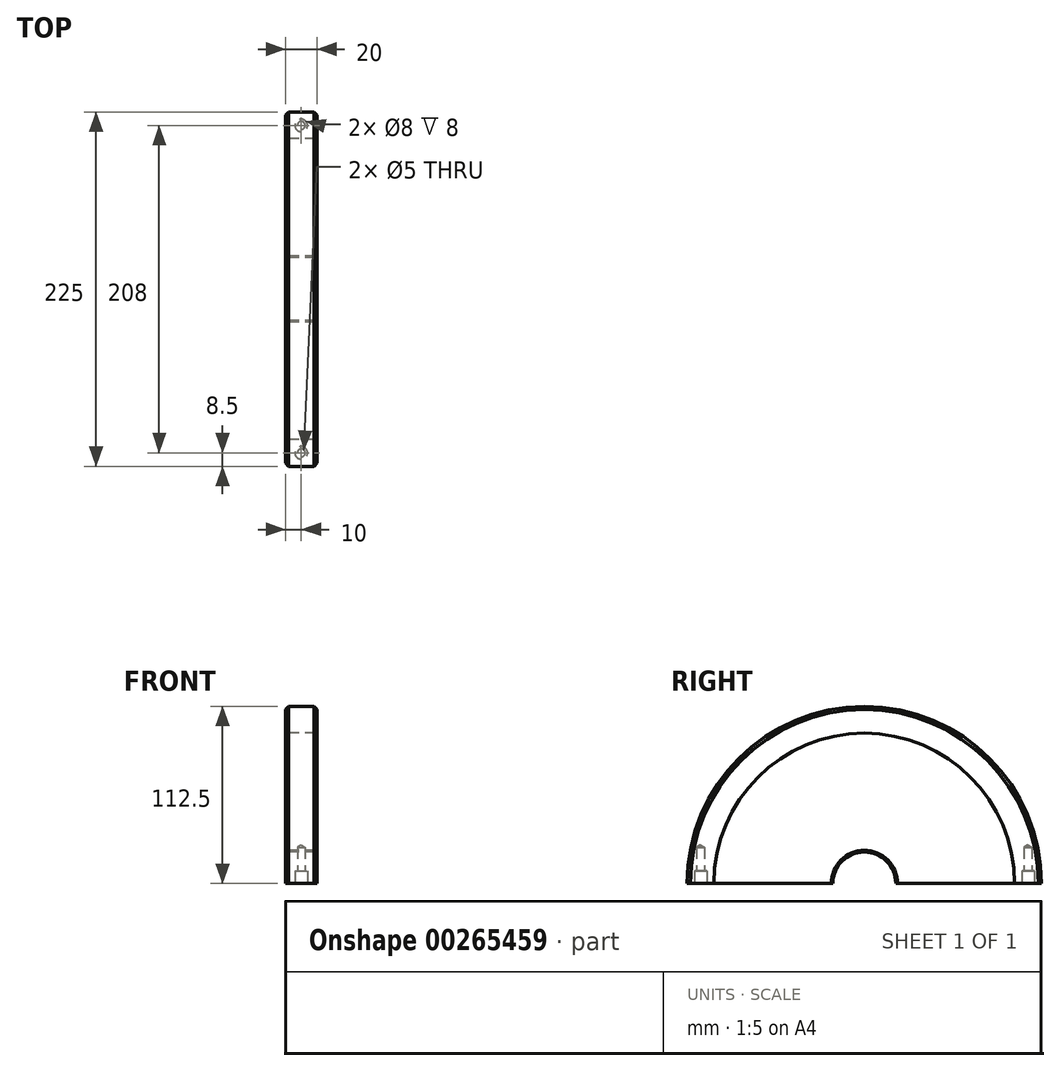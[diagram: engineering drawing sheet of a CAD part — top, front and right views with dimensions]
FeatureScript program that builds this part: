
annotation { "Feature Type Name" : "Feature", "Feature Type Description" : "" }
export const myFeature = defineFeature(function(context is Context, id is Id, definition is map)
    precondition{}
    {
        {
            var Q0;
            Q0=qCreatedBy(makeId("Front.planeOp"),FACE);
            var sketch = newSketch(context, id + "F0", { "sketchPlane" : qUnion([Q0])});
            skLineSegment(sketch, "E0", {"start": v(-48.97, 0) * mm, "end": v(48.97, 0) * mm, "construction": true});
            skLineSegment(sketch, "E1.bottom", {"start": v(-10, 21) * mm, "end": v(10, 21) * mm});
            skLineSegment(sketch, "E1.top", {"start": v(-10, 20) * mm, "end": v(10, 20) * mm});
            skLineSegment(sketch, "E1.left", {"start": v(-10, 21) * mm, "end": v(-10, 20) * mm});
            skLineSegment(sketch, "E1.right", {"start": v(10, 21) * mm, "end": v(10, 20) * mm});
            skLineSegment(sketch, "E2", {"start": v(0, 12.38) * mm, "end": v(0, -12.38) * mm, "construction": true});
            skSolve(sketch);
        }
        {
            var Q0;
            Q0=makeQuery(id+"F0.imprint","IMPRINT",FACE,{"disambiguationData":[TD([[makeQuery(id+"F0.imprint","IMPRINT",EDGE,{"derivedFrom":sQuery(id+"F0.wireOp",EDGE,"E1.bottom")}),-1.0]])]});
            var Q1;
            Q1=sQuery(id+"F0.wireOp",EDGE,"E0");
            revolve(context, id + "F1", {"entities" : qUnion([Q0]), "axis" : qUnion([Q1]), "revolveType" : RevolveType.FULL});
        }
        {
            var Q0;
            Q0=qCreatedBy(makeId("Front.planeOp"),FACE);
            var sketch = newSketch(context, id + "F2", { "sketchPlane" : qUnion([Q0])});
            skLineSegment(sketch, "E3.bottom", {"start": v(-10, 95.5) * mm, "end": v(10, 95.5) * mm});
            skLineSegment(sketch, "E3.top", {"start": v(-10, 21) * mm, "end": v(10, 21) * mm});
            skLineSegment(sketch, "E3.left", {"start": v(-10, 95.5) * mm, "end": v(-10, 21) * mm});
            skLineSegment(sketch, "E3.right", {"start": v(10, 95.5) * mm, "end": v(10, 21) * mm});
            skLineSegment(sketch, "E4", {"start": v(-46.04, 0) * mm, "end": v(46.04, 0) * mm, "construction": true});
            skSolve(sketch);
        }
        {
            var Q0;
            Q0=makeQuery(id+"F2.imprint","IMPRINT",FACE,{"disambiguationData":[TD([[makeQuery(id+"F2.imprint","IMPRINT",EDGE,{"derivedFrom":sQuery(id+"F2.wireOp",EDGE,"E3.bottom")}),-1.0]])]});
            var Q1;
            Q1=sQuery(id+"F2.wireOp",EDGE,"E4");
            revolve(context, id + "F3", {"entities" : qUnion([Q0]), "axis" : qUnion([Q1]), "revolveType" : RevolveType.FULL});
        }
        {
            var Q0;
            Q0=qCreatedBy(makeId("Front.planeOp"),FACE);
            var sketch = newSketch(context, id + "F4", { "sketchPlane" : qUnion([Q0])});
            skLineSegment(sketch, "E5", {"start": v(-40.4, 0) * mm, "end": v(40.4, 0) * mm, "construction": true});
            skLineSegment(sketch, "E6.bottom", {"start": v(-10, 112.5) * mm, "end": v(10, 112.5) * mm});
            skLineSegment(sketch, "E6.top", {"start": v(-10, 95.5) * mm, "end": v(10, 95.5) * mm});
            skLineSegment(sketch, "E6.left", {"start": v(-10, 112.5) * mm, "end": v(-10, 95.5) * mm});
            skLineSegment(sketch, "E6.right", {"start": v(10, 112.5) * mm, "end": v(10, 95.5) * mm});
            skSolve(sketch);
        }
        {
            var Q0;
            Q0=makeQuery(id+"F4.imprint","IMPRINT",FACE,{"disambiguationData":[TD([[makeQuery(id+"F4.imprint","IMPRINT",EDGE,{"derivedFrom":sQuery(id+"F4.wireOp",EDGE,"E6.bottom")}),-1.0]])]});
            var Q1;
            Q1=sQuery(id+"F4.wireOp",EDGE,"E5");
            revolve(context, id + "F5", {"entities" : qUnion([Q0]), "axis" : qUnion([Q1]), "revolveType" : RevolveType.FULL});
        }
        {
            var Q0;
            Q0=qCreatedBy(makeId("Right.planeOp"),FACE);
            var sketch = newSketch(context, id + "F6", { "sketchPlane" : qUnion([Q0])});
            skLineSegment(sketch, "E7", {"start": v(-50, 95.16) * mm, "end": v(-50, 125.78) * mm});
            skLineSegment(sketch, "E8", {"start": v(-30, 145.78) * mm, "end": v(30, 145.78) * mm});
            skLineSegment(sketch, "E9", {"start": v(50, 125.78) * mm, "end": v(50, 95.16) * mm});
            skPoint(sketch, "E10.visualSharp", {"position": v(50, 145.78) * mm});
            skArc(sketch, "E10.filletArc", {"start": v(50, 125.78) * mm, "mid": v(44.14, 139.92) * mm, "end": v(30, 145.78) * mm});
            skPoint(sketch, "E11.visualSharp", {"position": v(-50, 145.78) * mm});
            skArc(sketch, "E11.filletArc", {"start": v(-30, 145.78) * mm, "mid": v(-44.14, 139.92) * mm, "end": v(-50, 125.78) * mm});
            skPoint(sketch, "E12", {"position": v(50, 100.78) * mm});
            skSolve(sketch);
        }
        {
            var Q0;
            Q0=qCreatedBy(makeId("Top.planeOp"),FACE);
            var Q1;
            Q1=sQuery(id+"F6.wireOp",VERTEX,"E7.start");
            cPlane(context, id + "F7", {"entities" : qUnion([Q0, Q1]), "cplaneType" : CPlaneType.PLANE_POINT, "offset" : 25 * mm, "width" : 150 * mm, "height" : 150 * mm});
        }
        {
            var Q0;
            Q0=makeQuery(id+"F5.opRevolve","SWEPT_EDGE",EDGE,{"disambiguationData":[OSD([sQuery(id+"F4.wireOp",EDGE,"E6.bottom"),sQuery(id+"F4.wireOp",EDGE,"E6.right")])]});
            var Q1;
            Q1=makeQuery(id+"F5.opRevolve","SWEPT_EDGE",EDGE,{"disambiguationData":[OSD([sQuery(id+"F4.wireOp",EDGE,"E6.bottom"),sQuery(id+"F4.wireOp",EDGE,"E6.left")])]});
            chamfer(context, id + "F8", {"entities" : qUnion([Q0, Q1]), "width" : 2 * mm, "tangentPropagation" : true});
        }
        {
            var Q0;
            Q0=qCreatedBy(makeId("Front.planeOp"),FACE);
            var sketch = newSketch(context, id + "F9", { "sketchPlane" : qUnion([Q0])});
            skLineSegment(sketch, "E13.bottom", {"start": v(-10, 0) * mm, "end": v(10, 0) * mm});
            skLineSegment(sketch, "E13.top", {"start": v(-10, -115) * mm, "end": v(10, -115) * mm});
            skLineSegment(sketch, "E13.left", {"start": v(-10, 0) * mm, "end": v(-10, -115) * mm});
            skLineSegment(sketch, "E13.right", {"start": v(10, 0) * mm, "end": v(10, -115) * mm});
            skSolve(sketch);
        }
        {
            var Q0;
            Q0=qSketchRegion(id+"F9",true);
            extrude(context, id + "F10", {"entities" : qUnion([Q0]), "operationType" : NewBodyOperationType.REMOVE, "endBound" : BoundingType.THROUGH_ALL, "depth" : 25 * mm, "hasSecondDirection" : true, "secondDirectionBound" : SecondDirectionBoundingType.THROUGH_ALL, "secondDirectionOppositeDirection" : true, "secondDirectionDepth" : 25 * mm});
        }
        {
            var Q0;
            {var subQ0=sQuery(id+"F4.wireOp",EDGE,"E6.right");var subQ1=sQuery(id+"F4.wireOp",EDGE,"E6.left");var subQ2=sQuery(id+"F4.wireOp",EDGE,"E6.bottom");Q0=makeQuery(id+"F10.boolean.opBoolean","COPY",FACE,{"disambiguationData":[TD([makeQuery(id+"F5.opRevolve","SWEPT_FACE",FACE,{"disambiguationData":[OSD([subQ2])]}),makeQuery(id+"F5.opRevolve","SWEPT_FACE",FACE,{"disambiguationData":[OSD([sQuery(id+"F4.wireOp",EDGE,"E6.top")])]}),makeQuery(id+"F5.opRevolve","SWEPT_FACE",FACE,{"disambiguationData":[OSD([subQ1])]}),makeQuery(id+"F5.opRevolve","SWEPT_FACE",FACE,{"disambiguationData":[OSD([subQ0])]}),makeQuery(id+"F8.opChamfer","BLEND_FACE",FACE,{"disambiguationData":[OSD([subQ2,subQ1])]}),makeQuery(id+"F8.opChamfer","BLEND_FACE",FACE,{"disambiguationData":[OSD([subQ2,subQ0])]})]),OD(0.0)],"derivedFrom":makeQuery(id+"F10.opExtrude","SWEPT_FACE",FACE,{"disambiguationData":[OSD([sQuery(id+"F9.wireOp",EDGE,"E13.bottom")])]})});}
            var sketch = newSketch(context, id + "F11", { "sketchPlane" : qUnion([Q0])});
            skCircle(sketch, "E14", {"center": v(0, 104) * mm, "radius": 4 * mm});
            skLineSegment(sketch, "E15", {"start": v(0, 112.5) * mm, "end": v(0, 95.5) * mm, "construction": true});
            skPoint(sketch, "E16.MirrorP", {"position": v(0, -104) * mm});
            skCircle(sketch, "E17.MirrorC", {"center": v(0, -104) * mm, "radius": 4 * mm});
            skSolve(sketch);
        }
        {
            var Q0;
            Q0=qSketchRegion(id+"F11",true);
            extrude(context, id + "F12", {"entities" : qUnion([Q0]), "operationType" : NewBodyOperationType.REMOVE, "oppositeDirection" : true, "depth" : 8 * mm});
        }
        {
            var Q0;
            Q0=makeQuery(id+"F12.boolean.opBoolean","COPY",FACE,{"derivedFrom":makeQuery(id+"F12.opExtrude","CAP_FACE",FACE,{"disambiguationData":[OSD([sQuery(id+"F11.wireOp",EDGE,"E14")])],"isStart":false})});
            var sketch = newSketch(context, id + "F13", { "sketchPlane" : qUnion([Q0])});
            skPoint(sketch, "E18.0", {"position": v(0, 104) * mm});
            skPoint(sketch, "E18.1", {"position": v(0, -104) * mm});
            skSolve(sketch);
        }
        {
            var Q0;
            Q0=sQuery(id+"F13.wireOp",VERTEX,"E18.0");
            var Q1;
            Q1=sQuery(id+"F13.wireOp",VERTEX,"E18.1");
            var Q2;
            Q2=makeQuery(id+"F5.opRevolve","SWEPT_BODY",BODY,{"disambiguationData":[OSD([sQuery(id+"F4.wireOp",EDGE,"E6.bottom"),sQuery(id+"F4.wireOp",EDGE,"E6.top"),sQuery(id+"F4.wireOp",EDGE,"E6.left"),sQuery(id+"F4.wireOp",EDGE,"E6.right")])]});
            hole(context, id + "F14", {"style" : HoleStyle.SIMPLE, "endStyle" : HoleEndStyle.BLIND, "standardTappedOrClearance" : lookupTablePath({ "standard" : "ISO", "engagement" : "75%", "pitch" : "1 mm", "size" : "M6", "type" : "Tapped" }), "standardBlindInLast" : lookupTablePath({ "standard" : "ISO", "engagement" : "75%", "pitch" : "1 mm", "size" : "M6", "type" : "Tapped" }), "holeDiameter" : 5 * mm, "showTappedDepth" : true, "holeDepth" : 15 * mm, "tappedDepth" : 12 * mm, "tapClearance" : 3, "locations" : qUnion([Q0, Q1]), "scope" : qUnion([Q2]), "majorDiameter" : 6 * mm});
        }
    });
